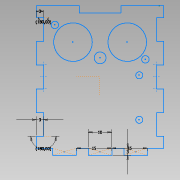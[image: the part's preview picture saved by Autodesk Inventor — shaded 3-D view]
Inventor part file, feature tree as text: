
AUTODESK INVENTOR PART (.ipt)
format: ipt  version: 2015 SP1 (Build 190203100, 203)  size: 87,040 bytes
history: native  units: mm
features: sketch x1
ambient origin geometry x8: Origin, YZ Plane, XZ Plane, XY Plane, X Axis, Y Axis, Z Axis, Center Point
feature tree (1):
  sketch  "Sketch1"  dims[d0=10.0mm d1=3.0mm d2=20.0mm d4=15.0mm d5=20.0mm d7=15.0mm d13=3.0mm d14=180.0deg d15=3.0mm d16=180.0deg]
